# Revit family: BOS-Oberlicht-Seitenteilzarge-osd-STW_Familie
name_source: partatom
category: Türen
revit_build: Autodesk Revit 2017 (Build: 20160225_1515(x64)
units: mm (PartAtom-declared; Revit-internal decimal feet)

## family parameters
Basisbauteil = Wand
Beim Laden mit Abzugskörper schneiden = Nein
Gemeinsam genutzt = Nein
Immer vertikal = Ja
Raumberechnungspunkt = Ja

## types (5) — shared parameters
AK-Aussteifungsprofilabstand = 104 mm  [stored 0.341207 ft]
Aluminiumglasleistenbreite = 12 mm  [stored 0.0393701 ft]
Aluminiumglasleistenhöhe = 15 mm  [stored 0.0492126 ft]
BBL1 Bandbezugslinie   Hinge Position 1 = 241 mm  [stored 0.790682 ft]
BE max. = 100 mm  [stored 0.328084 ft]
Bauelement = BOS Stahlzarge
Blechstärke = 2 mm  [stored 0.00656168 ft]
Drehpunkt Warnung sichtbar = Ja
Drehpunktreferenz = 500 mm  [stored 1.64042 ft]
Einfügepunkt = 54 mm  [stored 0.177165 ft]
FMB Seitenteil max. = 1000 mm  [stored 3.28084 ft]
FMB Seitenteil min. = 100 mm  [stored 0.328084 ft]
FMB Türblatt max. = 966 mm  [stored 3.16929 ft]
FMB Türblatt min. = 591 mm  [stored 1.93898 ft]
FMH Oberlicht min. = 95 mm
FMH Türblatt max. = 2233 mm
FMH Türblatt min. = 1608 mm  [stored 5.27559 ft]
Falzaufschlag = 15 mm  [stored 0.0492126 ft]
Falztiefe = 46.5 mm  [stored 0.152559 ft]
Falztiefe 2 = 25 mm  [stored 0.082021 ft]
Funktion = Innen
Gefälzt = Nein
Hersteller = BOS GmbH Best Of Steel, Lütkenfelde 4, D-48282 Emsdetten
Info-Texte sichtbar = Ja
Information in English = Nein
Kämpferblechstärke = 1.5 mm  [stored 0.00492126 ft]
Leibungstiefe Kämpfer max. = 40 mm  [stored 0.131234 ft]
Leibungstiefe Kämpfer min. = 40 mm  [stored 0.131234 ft]
MW max. = 330 mm  [stored 1.08268 ft]
Material = grundiert, feuerverzinktes Feinblech nach DIN EN 10143
Material - Acrylfuge = <Nach Kategorie>
Material - Bänder = <Nach Kategorie>
Material - Dichtung = <Nach Kategorie>
Material - Drückergarnitur = <Nach Kategorie>
Material - Eckabdeckung = <Nach Kategorie>
Material - Glasleisten = <Nach Kategorie>
Material - Türblatt = <Nach Kategorie>
Material - Verglasung = Glas
Material - Vorlegeband = <Nach Kategorie>
Material - Zarge = <Nach Kategorie>
Putzwinkel max. = 3 mm  [stored 0.00984252 ft]
Putzwinkel min. = 3 mm  [stored 0.00984252 ft]
Sickentiefe = 10 mm  [stored 0.0328084 ft]
Spiegel hinten max. = 4 mm  [stored 0.0131234 ft]
Spiegel hinten min. = 4 mm  [stored 0.0131234 ft]
Spiegel vorne max. = 4 mm  [stored 0.0131234 ft]
Spiegel vorne min. = 4 mm  [stored 0.0131234 ft]
Stumpf = Ja
Technische Infos rund um die Stahlzarge = www.BestOfSteel.de/tools-downloads/technische-infos-rund-um-die-stahlzarge/
Türblattabstand 2 = 4.5 mm  [stored 0.0147638 ft]
Türblattabstand 3 = 4.5 mm  [stored 0.0147638 ft]
Türblattabstand links-rechts = 3.5 mm  [stored 0.0114829 ft]
Türblattabstand oben = 4 mm  [stored 0.0131234 ft]
Türblattabstand unten = 7 mm  [stored 0.0229659 ft]
Türblattaufschlag = 13 mm
URL = www.BestOfSteel.de/stahlzargen/zargen-fuer-drehfluegeltueren/elementzargen/oberlicht-seitenteilzargen/
Öffnungswinkel max. = 180.00°
Öffnungswinkel min. = 0.00°
zero-valued in all types: Breite, Dicke, Rohbaubreite, Rohbauhöhe, Türblattstärke 1

## per-type parameters (varying)
- osd/KEsd mit Holztürblatt (Bandrolle sichtbar): 060-61/100 Bänder=Nein; Beschreibung=Oberlicht-/Seitenteilzarge als Sino-Zarge für Ständerwerk, stumpf; Doppelfalz=Nein; Drehpunktabstand (FM) horizontal=-5 mm  [stored -0.0164042 ft]; Drehpunktabstand (SP) vertikal=7.5 mm  [stored 0.0246063 ft]; Drückergarnitur=Ja; Einfachfalz=Ja; Falzaufschlag gesamt=15 mm  [stored 0.0492126 ft]; Falztiefe gesamt=46.5 mm  [stored 0.152559 ft]; Glastürblatt=Nein; Glastürdrücker=Nein; Gracila Bänder=Ja; Holztürblatt=Ja; MW min.=100 mm  [stored 0.328084 ft]; Modell=osd/KEsd; Rohrglasleistenbreite=10 mm  [stored 0.0328084 ft]; Rohrglasleistenhöhe=15 mm  [stored 0.0492126 ft]; Rohrglasleistenprofilverschiebung horizontal=7.5 mm  [stored 0.0246063 ft]; Rohrglasleistenprofilverschiebung vertikal=-5 mm  [stored -0.0164042 ft]; Tectus Bänder=Nein; Türblattabstand 1=-2 mm  [stored -0.00656168 ft]; Türblattstärke=40 mm  [stored 0.131234 ft]; Türblattstärke 2=40 mm  [stored 0.131234 ft]; Türblattstärke 3=0 mm  [stored 0 ft]; Türblattversatz  horizontal=-1.5 mm  [stored -0.00492126 ft]; Türblattversatz vertikal=9.5 mm  [stored 0.031168 ft]; osFd/KEsFd mit Holztürblatt (Bandrolle sichtbar)=Nein; osFd/KEsFd mit Holztürblatt (verdeckt liegendes Band)=Nein; osd/KEsd mit Glastürblatt=Nein; osd/KEsd mit Holztürblatt (Bandrolle sichtbar)=Ja; osd/KEsd mit Holztürblatt (verdeckt liegendes Band)=Nein
- osFd/KEsFd mit Holztürblatt (Bandrolle sichtbar): 060-61/100 Bänder=Nein; Beschreibung=Oberlicht-/Seitenteilzarge als Sino-Zarge für Ständerwerk, stumpf, mit Doppelfalz; Doppelfalz=Ja; Drehpunktabstand (FM) horizontal=-5 mm  [stored -0.0164042 ft]; Drehpunktabstand (SP) vertikal=7.5 mm  [stored 0.0246063 ft]; Drückergarnitur=Ja; Einfachfalz=Nein; Falzaufschlag gesamt=30 mm  [stored 0.0984252 ft]; Falztiefe gesamt=71.5 mm; Glastürblatt=Nein; Glastürdrücker=Nein; Gracila Bänder=Ja; Holztürblatt=Ja; MW min.=125 mm  [stored 0.410105 ft]; Modell=osFd/KEsFd; Rohrglasleistenbreite=15 mm  [stored 0.0492126 ft]; Rohrglasleistenhöhe=30 mm  [stored 0.0984252 ft]; Rohrglasleistenprofilverschiebung horizontal=15 mm  [stored 0.0492126 ft]; Rohrglasleistenprofilverschiebung vertikal=-7.5 mm  [stored -0.0246063 ft]; Tectus Bänder=Nein; Türblattabstand 1=-2 mm  [stored -0.00656168 ft]; Türblattstärke=65 mm  [stored 0.213255 ft]; Türblattstärke 2=40 mm  [stored 0.131234 ft]; Türblattstärke 3=25 mm  [stored 0.082021 ft]; Türblattversatz  horizontal=-1.5 mm  [stored -0.00492126 ft]; Türblattversatz vertikal=9.5 mm  [stored 0.031168 ft]; osFd/KEsFd mit Holztürblatt (Bandrolle sichtbar)=Ja; osFd/KEsFd mit Holztürblatt (verdeckt liegendes Band)=Nein; osd/KEsd mit Glastürblatt=Nein; osd/KEsd mit Holztürblatt (Bandrolle sichtbar)=Nein; osd/KEsd mit Holztürblatt (verdeckt liegendes Band)=Nein
- osd/KEsd mit Holztürblatt (verdeckt liegendes Band): 060-61/100 Bänder=Nein; Beschreibung=Oberlicht-/Seitenteilzarge als Sino-Zarge für Ständerwerk, stumpf; Doppelfalz=Nein; Drehpunktabstand (FM) horizontal=-5 mm  [stored -0.0164042 ft]; Drehpunktabstand (SP) vertikal=7.5 mm  [stored 0.0246063 ft]; Drückergarnitur=Ja; Einfachfalz=Ja; Falzaufschlag gesamt=15 mm  [stored 0.0492126 ft]; Falztiefe gesamt=46.5 mm  [stored 0.152559 ft]; Glastürblatt=Nein; Glastürdrücker=Nein; Gracila Bänder=Nein; Holztürblatt=Ja; MW min.=100 mm  [stored 0.328084 ft]; Modell=osd/KEsd; Rohrglasleistenbreite=10 mm  [stored 0.0328084 ft]; Rohrglasleistenhöhe=15 mm  [stored 0.0492126 ft]; Rohrglasleistenprofilverschiebung horizontal=7.5 mm  [stored 0.0246063 ft]; Rohrglasleistenprofilverschiebung vertikal=-5 mm  [stored -0.0164042 ft]; Tectus Bänder=Ja; Türblattabstand 1=-2 mm  [stored -0.00656168 ft]; Türblattstärke=40 mm  [stored 0.131234 ft]; Türblattstärke 2=40 mm  [stored 0.131234 ft]; Türblattstärke 3=0 mm  [stored 0 ft]; Türblattversatz  horizontal=-1.5 mm  [stored -0.00492126 ft]; Türblattversatz vertikal=9.5 mm  [stored 0.031168 ft]; osFd/KEsFd mit Holztürblatt (Bandrolle sichtbar)=Nein; osFd/KEsFd mit Holztürblatt (verdeckt liegendes Band)=Nein; osd/KEsd mit Glastürblatt=Nein; osd/KEsd mit Holztürblatt (Bandrolle sichtbar)=Nein; osd/KEsd mit Holztürblatt (verdeckt liegendes Band)=Ja
- osFd/KEsFd mit Holztürblatt (verdeckt liegendes Band): 060-61/100 Bänder=Nein; Beschreibung=Oberlicht-/Seitenteilzarge als Sino-Zarge für Ständerwerk, stumpf, mit Doppelfalz; Doppelfalz=Ja; Drehpunktabstand (FM) horizontal=-5 mm  [stored -0.0164042 ft]; Drehpunktabstand (SP) vertikal=7.5 mm  [stored 0.0246063 ft]; Drückergarnitur=Ja; Einfachfalz=Nein; Falzaufschlag gesamt=30 mm  [stored 0.0984252 ft]; Falztiefe gesamt=71.5 mm; Glastürblatt=Nein; Glastürdrücker=Nein; Gracila Bänder=Nein; Holztürblatt=Ja; MW min.=125 mm  [stored 0.410105 ft]; Modell=osFd/KEsFd; Rohrglasleistenbreite=15 mm  [stored 0.0492126 ft]; Rohrglasleistenhöhe=30 mm  [stored 0.0984252 ft]; Rohrglasleistenprofilverschiebung horizontal=15 mm  [stored 0.0492126 ft]; Rohrglasleistenprofilverschiebung vertikal=-7.5 mm  [stored -0.0246063 ft]; Tectus Bänder=Ja; Türblattabstand 1=-2 mm  [stored -0.00656168 ft]; Türblattstärke=65 mm  [stored 0.213255 ft]; Türblattstärke 2=40 mm  [stored 0.131234 ft]; Türblattstärke 3=25 mm  [stored 0.082021 ft]; Türblattversatz  horizontal=-1.5 mm  [stored -0.00492126 ft]; Türblattversatz vertikal=9.5 mm  [stored 0.031168 ft]; osFd/KEsFd mit Holztürblatt (Bandrolle sichtbar)=Nein; osFd/KEsFd mit Holztürblatt (verdeckt liegendes Band)=Ja; osd/KEsd mit Glastürblatt=Nein; osd/KEsd mit Holztürblatt (Bandrolle sichtbar)=Nein; osd/KEsd mit Holztürblatt (verdeckt liegendes Band)=Nein
- osd/KEsd mit Glastürblatt: 060-61/100 Bänder=Ja; Beschreibung=Oberlicht-/Seitenteilzarge als Sino-Zarge für Ständerwerk, stumpf; Doppelfalz=Nein; Drehpunktabstand (FM) horizontal=-2 mm  [stored -0.00656168 ft]; Drehpunktabstand (SP) vertikal=10.5 mm  [stored 0.0344488 ft]; Drückergarnitur=Nein; Einfachfalz=Ja; Falzaufschlag gesamt=15 mm  [stored 0.0492126 ft]; Falztiefe gesamt=46.5 mm  [stored 0.152559 ft]; Glastürblatt=Ja; Glastürdrücker=Ja; Gracila Bänder=Nein; Holztürblatt=Nein; MW min.=100 mm  [stored 0.328084 ft]; Modell=osd/KEsd; Rohrglasleistenbreite=10 mm  [stored 0.0328084 ft]; Rohrglasleistenhöhe=15 mm  [stored 0.0492126 ft]; Rohrglasleistenprofilverschiebung horizontal=7.5 mm  [stored 0.0246063 ft]; Rohrglasleistenprofilverschiebung vertikal=-5 mm  [stored -0.0164042 ft]; Tectus Bänder=Nein; Türblattabstand 1=-34 mm; Türblattstärke=8 mm  [stored 0.0262467 ft]; Türblattstärke 2=8 mm  [stored 0.0262467 ft]; Türblattstärke 3=0 mm  [stored 0 ft]; Türblattversatz  horizontal=1.5 mm  [stored 0.00492126 ft]; Türblattversatz vertikal=44.5 mm  [stored 0.145997 ft]; osFd/KEsFd mit Holztürblatt (Bandrolle sichtbar)=Nein; osFd/KEsFd mit Holztürblatt (verdeckt liegendes Band)=Nein; osd/KEsd mit Glastürblatt=Ja; osd/KEsd mit Holztürblatt (Bandrolle sichtbar)=Nein; osd/KEsd mit Holztürblatt (verdeckt liegendes Band)=Nein

note: [stored X ft] marks values corroborated as IEEE doubles in the binary element streams (Revit-internal decimal feet)

## geometry (parser evidence)
native form markers: Extrusion x4
no freeform markers — native parametric forms only
